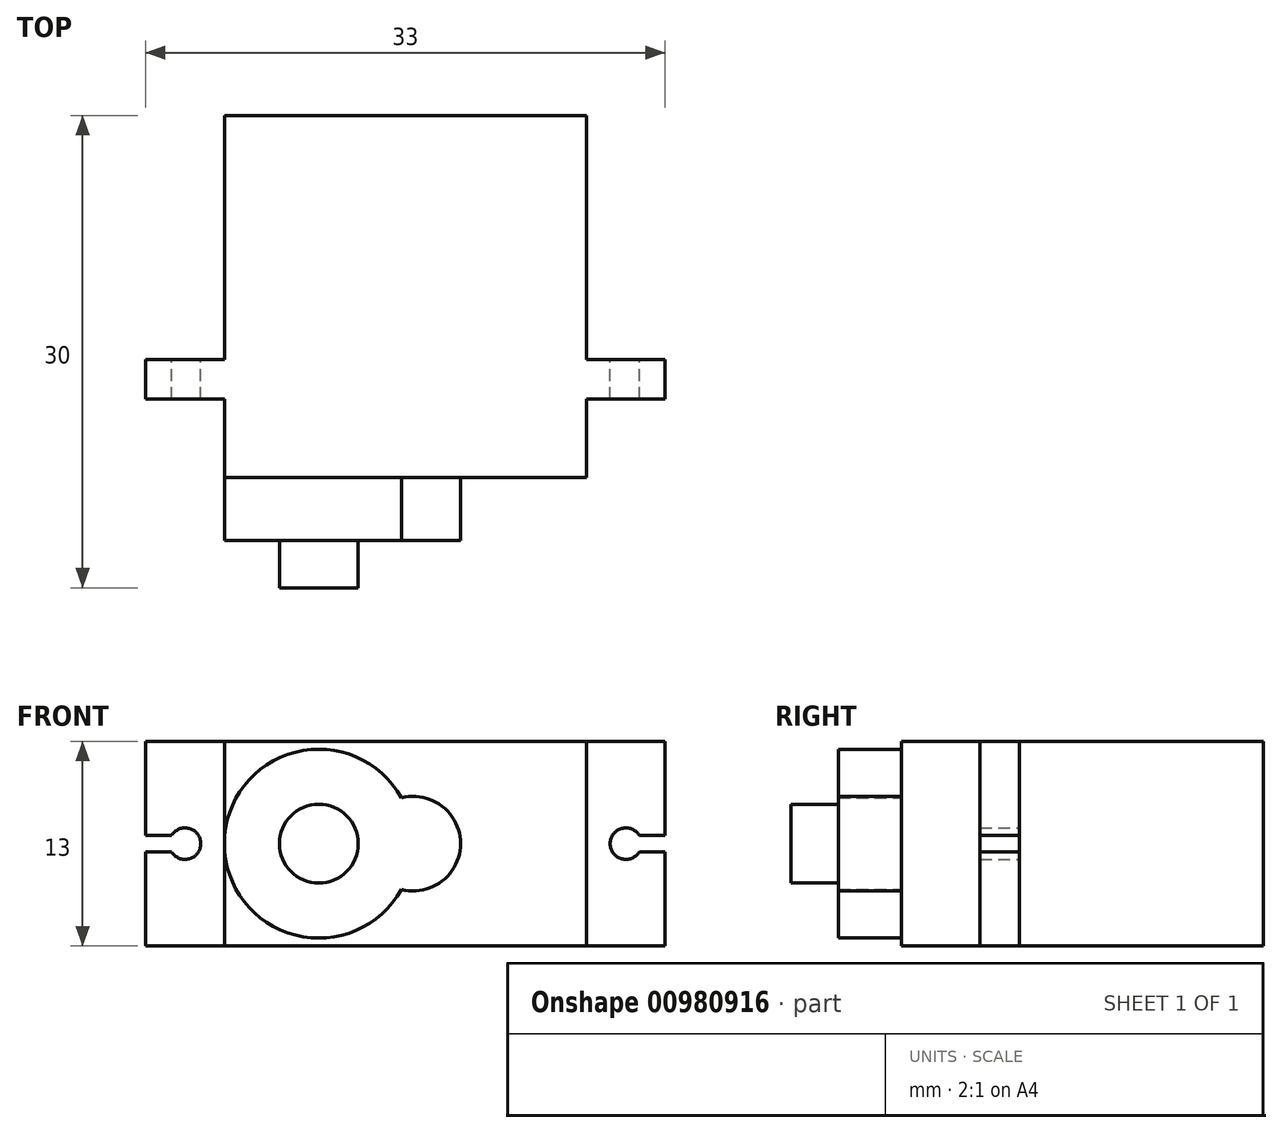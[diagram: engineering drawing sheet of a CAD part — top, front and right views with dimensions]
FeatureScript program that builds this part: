
annotation { "Feature Type Name" : "Feature", "Feature Type Description" : "" }
export const myFeature = defineFeature(function(context is Context, id is Id, definition is map)
    precondition{}
    {
        {
            var Q0;
            Q0=qCreatedBy(makeId("Front.planeOp"),FACE);
            var sketch = newSketch(context, id + "F0", { "sketchPlane" : qUnion([Q0])});
            skLineSegment(sketch, "E0.bottom", {"start": v(11.5, -6.5) * mm, "end": v(-11.5, -6.5) * mm});
            skLineSegment(sketch, "E0.top", {"start": v(11.5, 6.5) * mm, "end": v(-11.5, 6.5) * mm});
            skLineSegment(sketch, "E0.left", {"start": v(11.5, -6.5) * mm, "end": v(11.5, 6.5) * mm});
            skLineSegment(sketch, "E0.right", {"start": v(-11.5, -6.5) * mm, "end": v(-11.5, 6.5) * mm});
            skPoint(sketch, "E0.middle", {"position": v(0, 0) * mm});
            skLineSegment(sketch, "E1.bottom", {"start": v(11.5, 6.5) * mm, "end": v(16.5, 6.5) * mm});
            skLineSegment(sketch, "E1.top", {"start": v(11.5, -6.5) * mm, "end": v(16.5, -6.5) * mm});
            skLineSegment(sketch, "E1.left", {"start": v(11.5, 6.5) * mm, "end": v(11.5, -6.5) * mm});
            skLineSegment(sketch, "E1.right", {"start": v(16.5, 6.5) * mm, "end": v(16.5, -6.5) * mm});
            skCircle(sketch, "E2", {"center": v(14, 0) * mm, "radius": 1 * mm});
            skPoint(sketch, "E2.centerSnap0", {"position": v(14, 6.5) * mm});
            skCircle(sketch, "E3", {"center": v(-5.5, 0) * mm, "radius": 6 * mm});
            skCircle(sketch, "E4", {"center": v(0.5, 0) * mm, "radius": 3 * mm});
            skCircle(sketch, "E5", {"center": v(-5.5, 0) * mm, "radius": 2.5 * mm});
            skLineSegment(sketch, "E6", {"start": v(14.86, 0.51) * mm, "end": v(16.5, 0.51) * mm});
            skLineSegment(sketch, "E7", {"start": v(14.86, -0.51) * mm, "end": v(16.5, -0.51) * mm});
            skSolve(sketch);
        }
        {
            var Q0;
            {var subQ4=sQuery(id+"F0.wireOp",EDGE,"E0.bottom");Q0=makeQuery(id+"F0.imprint","IMPRINT",FACE,{"disambiguationData":[TD([[makeQuery(id+"F0.imprint","IMPRINT",EDGE,{"derivedFrom":subQ4}),-1.0]])]});}
            var Q1;
            {var subQ0=sQuery(id+"F0.wireOp",EDGE,"E4");var subQ1=sQuery(id+"F0.wireOp",EDGE,"E3");var subQ2=makeQuery(id+"F0.imprint","INTERSECT",VERTEX,{"disambiguationData":[OD(0.0)],"derivedFrom":[subQ1,subQ0]});Q1=makeQuery(id+"F0.imprint","IMPRINT",FACE,{"disambiguationData":[TD([[makeQuery(id+"F0.imprint","IMPRINT",EDGE,{"disambiguationData":[TD([[subQ2,1.0]])],"derivedFrom":subQ1}),-1.0]])]});}
            var Q2;
            {var subQ0=sQuery(id+"F0.wireOp",EDGE,"E4");var subQ1=sQuery(id+"F0.wireOp",EDGE,"E3");var subQ2=makeQuery(id+"F0.imprint","INTERSECT",VERTEX,{"disambiguationData":[OD(0.0)],"derivedFrom":[subQ1,subQ0]});Q2=makeQuery(id+"F0.imprint","IMPRINT",FACE,{"disambiguationData":[TD([[makeQuery(id+"F0.imprint","IMPRINT",EDGE,{"disambiguationData":[TD([[subQ2,1.0]])],"derivedFrom":subQ1}),1.0]])]});}
            var Q3;
            {var subQ0=sQuery(id+"F0.wireOp",EDGE,"E3");var subQ1=makeQuery(id+"F0.imprint","INTERSECT",VERTEX,{"derivedFrom":[sQuery(id+"F0.wireOp",EDGE,"E0.right"),subQ0]});Q3=makeQuery(id+"F0.imprint","IMPRINT",FACE,{"disambiguationData":[TD([[makeQuery(id+"F0.imprint","IMPRINT",EDGE,{"disambiguationData":[TD([[subQ1,1.0]])],"derivedFrom":subQ0}),1.0]])]});}
            extrude(context, id + "F1", {"entities" : qUnion([Q0, Q1, Q2, Q3]), "depth" : 23 * mm, "offsetDistance" : 25 * mm});
        }
        {
            var Q0;
            Q0=makeQuery(id+"F0.imprint","IMPRINT",FACE,{"disambiguationData":[TD([[makeQuery(id+"F0.imprint","IMPRINT",EDGE,{"derivedFrom":sQuery(id+"F0.wireOp",EDGE,"E1.bottom")}),-1.0]])]});
            extrude(context, id + "F2", {"entities" : qUnion([Q0]), "depth" : 18 * mm, "offsetDistance" : 25 * mm, "hasSecondDirection" : true, "secondDirectionOppositeDirection" : false, "secondDirectionDepth" : 15.5 * mm});
        }
        {
            var Q0;
            Q0=makeQuery(id+"F2.opExtrude","SWEPT_BODY",BODY,{"disambiguationData":[OSD([sQuery(id+"F0.wireOp",EDGE,"E1.bottom"),sQuery(id+"F0.wireOp",EDGE,"E1.top"),sQuery(id+"F0.wireOp",EDGE,"E1.left"),sQuery(id+"F0.wireOp",EDGE,"E1.right"),sQuery(id+"F0.wireOp",EDGE,"E2")])]});
            var Q1;
            Q1=qCreatedBy(makeId("Right.planeOp"),FACE);
            mirror(context, id + "F3", {"operationType" : NewBodyOperationType.ADD, "entities" : qUnion([Q0]), "mirrorPlane" : qUnion([Q1])});
        }
        {
            var Q0;
            {var subQ0=sQuery(id+"F0.wireOp",EDGE,"E3");var subQ1=makeQuery(id+"F0.imprint","INTERSECT",VERTEX,{"derivedFrom":[sQuery(id+"F0.wireOp",EDGE,"E0.right"),subQ0]});Q0=makeQuery(id+"F0.imprint","IMPRINT",FACE,{"disambiguationData":[TD([[makeQuery(id+"F0.imprint","IMPRINT",EDGE,{"disambiguationData":[TD([[subQ1,1.0]])],"derivedFrom":subQ0}),1.0]])]});}
            var Q1;
            {var subQ0=sQuery(id+"F0.wireOp",EDGE,"E4");var subQ1=sQuery(id+"F0.wireOp",EDGE,"E3");var subQ2=makeQuery(id+"F0.imprint","INTERSECT",VERTEX,{"disambiguationData":[OD(0.0)],"derivedFrom":[subQ1,subQ0]});Q1=makeQuery(id+"F0.imprint","IMPRINT",FACE,{"disambiguationData":[TD([[makeQuery(id+"F0.imprint","IMPRINT",EDGE,{"disambiguationData":[TD([[subQ2,1.0]])],"derivedFrom":subQ1}),-1.0]])]});}
            var Q2;
            {var subQ0=sQuery(id+"F0.wireOp",EDGE,"E4");var subQ1=sQuery(id+"F0.wireOp",EDGE,"E3");var subQ2=makeQuery(id+"F0.imprint","INTERSECT",VERTEX,{"disambiguationData":[OD(0.0)],"derivedFrom":[subQ1,subQ0]});Q2=makeQuery(id+"F0.imprint","IMPRINT",FACE,{"disambiguationData":[TD([[makeQuery(id+"F0.imprint","IMPRINT",EDGE,{"disambiguationData":[TD([[subQ2,1.0]])],"derivedFrom":subQ1}),1.0]])]});}
            extrude(context, id + "F4", {"entities" : qUnion([Q0, Q1, Q2]), "operationType" : NewBodyOperationType.ADD, "depth" : 27 * mm, "offsetDistance" : 25 * mm, "hasSecondDirection" : true, "secondDirectionOppositeDirection" : false, "secondDirectionDepth" : 23 * mm});
        }
        {
            var Q0;
            Q0=makeQuery(id+"F0.imprint","IMPRINT",FACE,{"disambiguationData":[TD([[makeQuery(id+"F0.imprint","IMPRINT",EDGE,{"derivedFrom":sQuery(id+"F0.wireOp",EDGE,"E5")}),1.0]])]});
            extrude(context, id + "F5", {"entities" : qUnion([Q0]), "operationType" : NewBodyOperationType.ADD, "depth" : 30 * mm, "offsetDistance" : 25 * mm});
        }
    });
